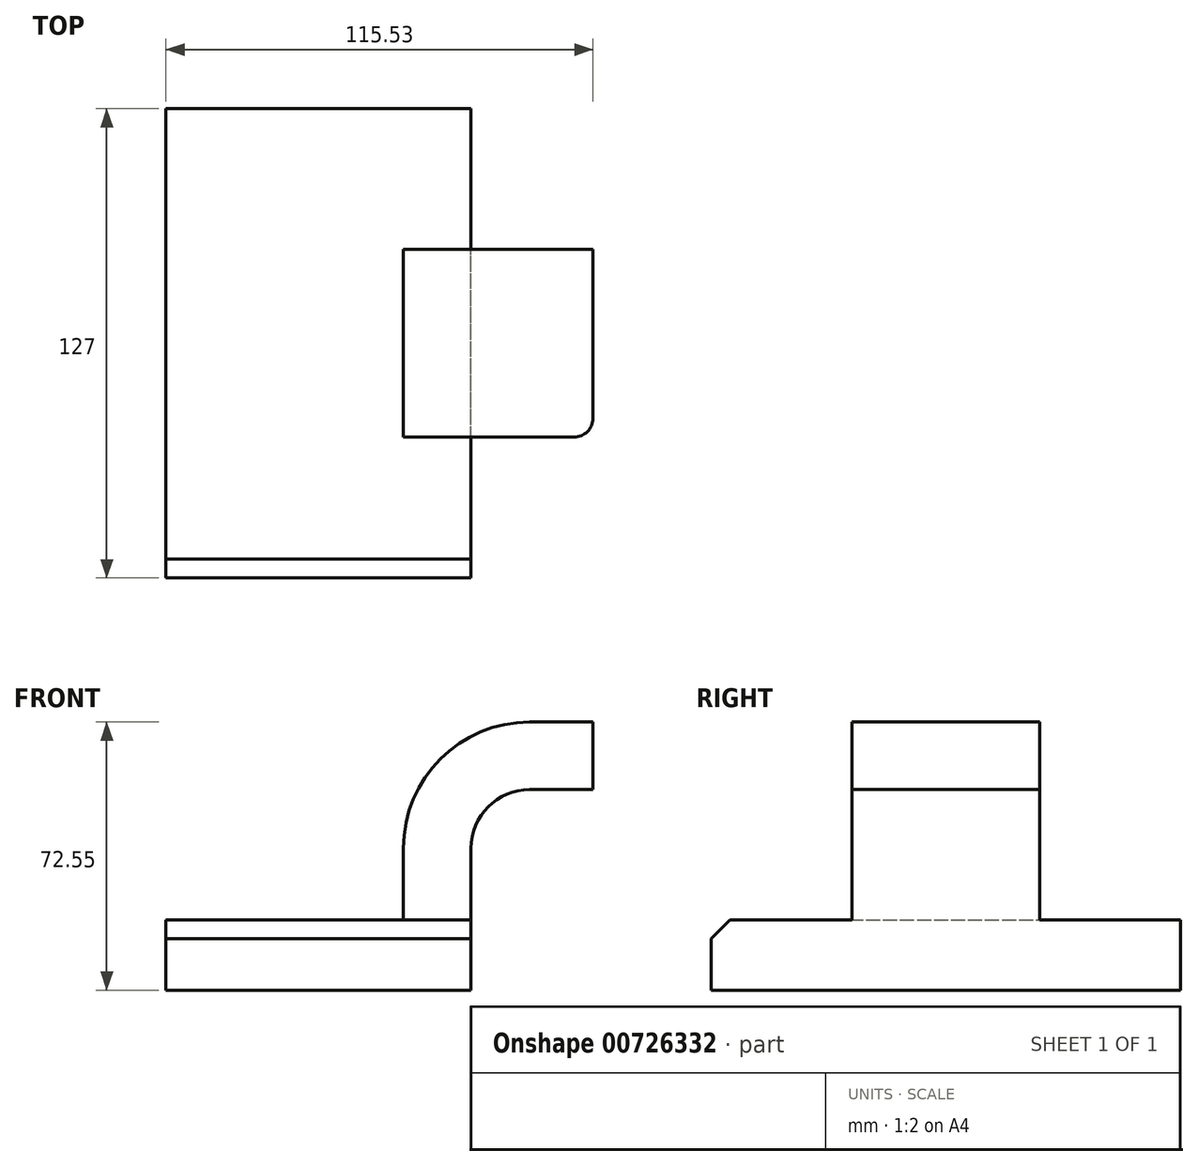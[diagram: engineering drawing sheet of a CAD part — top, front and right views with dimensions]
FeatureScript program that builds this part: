
annotation { "Feature Type Name" : "Feature", "Feature Type Description" : "" }
export const myFeature = defineFeature(function(context is Context, id is Id, definition is map)
    precondition{}
    {
        {
            var Q0;
            Q0=qCreatedBy(makeId("Front.planeOp"),FACE);
            var sketch = newSketch(context, id + "F0", { "sketchPlane" : qUnion([Q0])});
            skLineSegment(sketch, "E0.bottom", {"start": v(-41.28, 9.52) * mm, "end": v(41.27, 9.53) * mm});
            skLineSegment(sketch, "E0.top", {"start": v(-41.28, -9.53) * mm, "end": v(41.28, -9.53) * mm});
            skLineSegment(sketch, "E0.left", {"start": v(-41.28, 9.52) * mm, "end": v(-41.28, -9.53) * mm});
            skLineSegment(sketch, "E0.right", {"start": v(41.27, 9.53) * mm, "end": v(41.28, -9.52) * mm});
            skPoint(sketch, "E0.middle", {"position": v(0, 0) * mm});
            skLineSegment(sketch, "E1.bottom", {"start": v(60.32, 38.1) * mm, "end": v(111.12, 38.1) * mm});
            skLineSegment(sketch, "E1.top", {"start": v(60.32, 66.67) * mm, "end": v(111.12, 66.67) * mm});
            skLineSegment(sketch, "E1.left", {"start": v(60.32, 38.1) * mm, "end": v(60.32, 66.67) * mm});
            skLineSegment(sketch, "E1.right", {"start": v(111.12, 38.1) * mm, "end": v(111.12, 66.67) * mm});
            skPoint(sketch, "E1.middle", {"position": v(85.72, 52.39) * mm});
            skLineSegment(sketch, "E2", {"start": v(41.27, 9.53) * mm, "end": v(41.27, 28.86) * mm});
            skArc(sketch, "E3", {"start": v(41.27, 28.86) * mm, "mid": v(45.92, 40.08) * mm, "end": v(57.15, 44.73) * mm});
            skLineSegment(sketch, "E4", {"start": v(57.15, 44.73) * mm, "end": v(74.26, 44.73) * mm});
            skLineSegment(sketch, "E5.0", {"start": v(57.15, 43.97) * mm, "end": v(74.26, 43.97) * mm});
            skArc(sketch, "E5.1", {"start": v(42.04, 28.86) * mm, "mid": v(46.46, 39.54) * mm, "end": v(57.15, 43.97) * mm});
            skLineSegment(sketch, "E5.2", {"start": v(42.04, 9.53) * mm, "end": v(42.04, 28.86) * mm});
            skLineSegment(sketch, "E6.0", {"start": v(57.15, 63.02) * mm, "end": v(74.26, 63.02) * mm});
            skArc(sketch, "E6.1", {"start": v(22.99, 28.86) * mm, "mid": v(33, 53.01) * mm, "end": v(57.15, 63.02) * mm});
            skLineSegment(sketch, "E6.2", {"start": v(22.99, 9.53) * mm, "end": v(22.99, 28.86) * mm});
            skLineSegment(sketch, "E7", {"start": v(74.26, 66.67) * mm, "end": v(74.26, 38.1) * mm});
            skFitSpline(sketch, "E8", {"points": [v(-41.28, 9.52) * mm, v(60.32, 66.67) * mm], "startDerivative": vector(69.7, 122.95) * mm, "endDerivative": vector(106.46, 10.29) * mm});
            skSolve(sketch);
        }
        {
            var Q0;
            Q0=makeQuery(id+"F0.imprint","IMPRINT",FACE,{"disambiguationData":[TD([[makeQuery(id+"F0.imprint","IMPRINT",EDGE,{"derivedFrom":sQuery(id+"F0.wireOp",EDGE,"E0.top")}),1.0]])]});
            extrude(context, id + "F1", {"entities" : qUnion([Q0]), "endBound" : BoundingType.SYMMETRIC, "depth" : 127 * mm, "offsetDistance" : 25.4 * mm});
        }
        {
            var Q0;
            {var subQ1=sQuery(id+"F0.wireOp",EDGE,"E2");Q0=makeQuery(id+"F0.imprint","IMPRINT",FACE,{"disambiguationData":[TD([[makeQuery(id+"F0.imprint","IMPRINT",EDGE,{"derivedFrom":subQ1}),1.0]])]});}
            var Q1;
            {var subQ0=sQuery(id+"F0.wireOp",EDGE,"E4");var subQ1=sQuery(id+"F0.wireOp",EDGE,"E1.left");var subQ2=makeQuery(id+"F0.imprint","INTERSECT",VERTEX,{"derivedFrom":[subQ1,subQ0]});Q1=makeQuery(id+"F0.imprint","IMPRINT",FACE,{"disambiguationData":[TD([[makeQuery(id+"F0.imprint","IMPRINT",EDGE,{"disambiguationData":[TD([[subQ2,-1.0]])],"derivedFrom":subQ1}),-1.0]])]});}
            extrude(context, id + "F2", {"entities" : qUnion([Q0, Q1]), "operationType" : NewBodyOperationType.ADD, "endBound" : BoundingType.SYMMETRIC, "depth" : 50.8 * mm, "offsetDistance" : 25.4 * mm});
        }
        {
            var Q0;
            {var subQ0=sQuery(id+"F0.wireOp",EDGE,"E6.1");Q0=makeQuery(id+"F0.imprint","IMPRINT",FACE,{"disambiguationData":[TD([[makeQuery(id+"F0.imprint","IMPRINT",EDGE,{"derivedFrom":subQ0}),1.0]])]});}
            extrude(context, id + "F3", {"entities" : qUnion([Q0]), "operationType" : NewBodyOperationType.ADD, "depth" : 15.88 * mm, "offsetDistance" : 25.4 * mm});
        }
        {
            var Q0;
            Q0=makeQuery(id+"F1.opExtrude","CAP_EDGE",EDGE,{"disambiguationData":[OSD([sQuery(id+"F0.wireOp",EDGE,"E0.bottom")])],"isStart":false});
            chamfer(context, id + "F4", {"entities" : qUnion([Q0]), "width" : 5.08 * mm, "tangentPropagation" : true});
        }
        {
            var Q0;
            Q0=makeQuery(id+"F2.opExtrude","CAP_EDGE",EDGE,{"disambiguationData":[OSD([sQuery(id+"F0.wireOp",EDGE,"E7")])],"isStart":false});
            fillet(context, id + "F5", {"entities" : qUnion([Q0]), "radius" : 5.08 * mm, "tangentPropagation" : true, "allowEdgeOverflow" : false});
        }
    });
